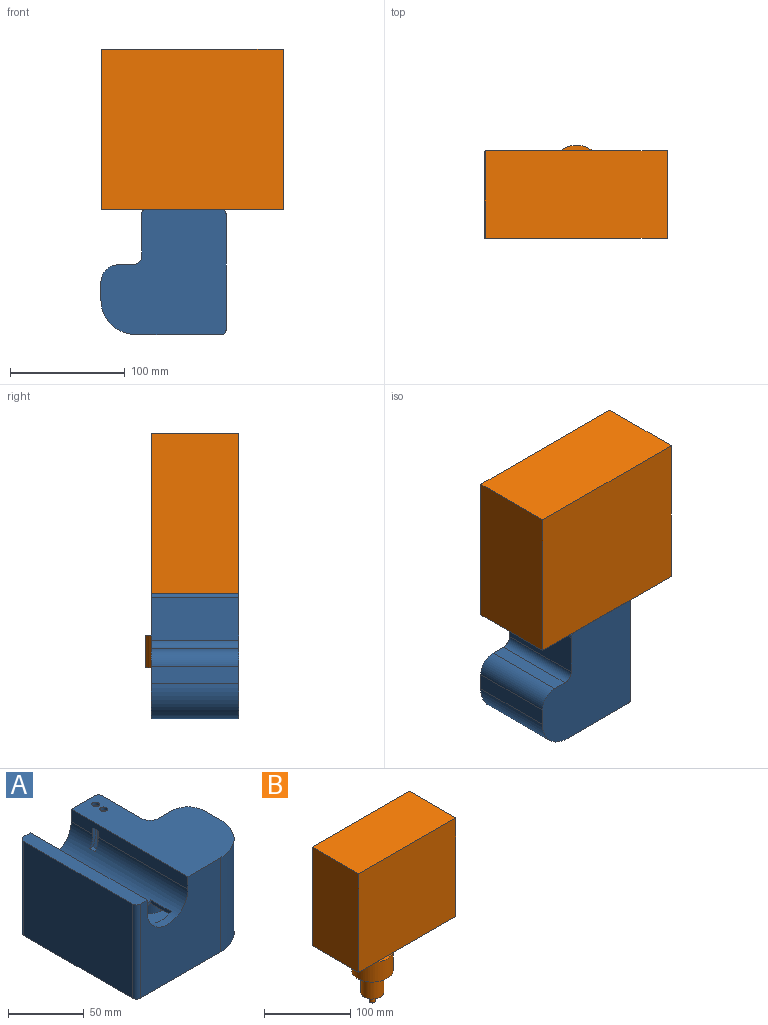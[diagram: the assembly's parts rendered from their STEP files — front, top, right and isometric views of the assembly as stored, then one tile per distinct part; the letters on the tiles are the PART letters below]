
ASSEMBLY  parts=2 mates=1
PART A: 46 faces, bbox 109.2x109.2x76.2 mm
  f0: cylinder r=21.59mm len=104.14mm, axis (0,1,0), area 6633.9mm2, adj f1,f5,f11,f19,f20,f21,f22,f23
  f1: plane 104.14x7.62mm, normal (1,0,0), area 767.7mm2, adj f0,f5,f11,f17,f43,f44,f45
  f2: cylinder r=19.05mm len=109.22mm, axis (0,1,0), area 6102.1mm2, adj f3,f20,f21,f22,f23,f25,f31,f39
  f3: plane 109.22x10.16mm, normal (-1,0,0), area 1083.9mm2, adj f2,f25,f31,f37,f43,f44,f45
  f4: plane 104.14x5.08mm, normal (0,0,-1), area 528.3mm2, adj f5,f8,f9,f10,f11,f19
  f5: plane 71.12x66.04mm, normal (0,-1,0), area 3635.5mm2, adj f0,f1,f4,f7,f8,f17,f18,f19
  f6: plane 71.12x36.83mm, normal (-1,0,0), area 2619.3mm2, adj f7,f16,f17,f18
  f7: cylinder r=1.27mm len=71.12mm, axis (0,0,-1), area 141.9mm2, adj f5,f6,f17,f18
  f8: cylinder r=1.27mm len=71.12mm, axis (0,0,-1), area 141.9mm2, adj f4,f5,f9,f18
  f9: plane 101.6x71.12mm, normal (1,0,0), area 7225.8mm2, adj f4,f8,f10,f18
  f10: cylinder r=1.27mm len=71.12mm, axis (0,0,-1), area 141.9mm2, adj f4,f9,f11,f18
  f11: plane 74.93x71.12mm, normal (0,1,0), area 4267.8mm2, adj f0,f1,f4,f10,f12,f17,f18,f19
  f12: cylinder r=27.94mm len=71.12mm, axis (0,0,-1), area 3121.3mm2, adj f11,f13,f17,f18
  f13: plane 71.12x15.24mm, normal (-1,0,0), area 1083.9mm2, adj f12,f14,f17,f18
  f14: cylinder r=12.7mm len=71.12mm, axis (0,0,-1), area 1418.8mm2, adj f13,f15,f17,f18
  f15: plane 71.12x12.7mm, normal (0,-1,0), area 903.2mm2, adj f14,f16,f17,f18
  f16: cylinder r=10.16mm len=71.12mm, axis (0,0,-1), area 1135mm2, adj f6,f15,f17,f18
  f17: plane 104.14x55.88mm, normal (0,0,-1), area 3882.3mm2, adj f1,f5,f6,f7,f11,f12,f13,f14
  f18: plane 104.14x104.14mm, normal (0,0,1), area 8948mm2, adj f5,f6,f7,f8,f9,f10,f11,f12
  f19: plane 104.14x7.62mm, normal (-1,0,0), area 793.5mm2, adj f0,f4,f5,f11
  f20: plane 19.05x2.88mm, normal (-1,0,0), area 54.8mm2, adj f0,f2,f21,f23
  f21: plane 19.05x5.09mm, normal (0,-1,0), area 50.4mm2, adj f0,f2,f20,f22
  f22: plane 19.05x2.88mm, normal (1,0,0), area 54.8mm2, adj f0,f2,f21,f23
  f23: plane 19.05x5.09mm, normal (0,1,0), area 50.4mm2, adj f0,f2,f20,f22
  f24: plane 109.22x10.16mm, normal (0,0,1), area 1103.4mm2, adj f25,f28,f29,f30,f31,f39
  f25: plane 76.2x66.04mm, normal (0,1,0), area 4075.1mm2, adj f2,f3,f24,f27,f28,f37,f38,f39
  f26: plane 76.2x36.83mm, normal (1,0,0), area 2806.4mm2, adj f27,f36,f37,f38
  f27: cylinder r=3.81mm len=76.2mm, axis (0,0,-1), area 456mm2, adj f25,f26,f37,f38
  f28: cylinder r=3.81mm len=76.2mm, axis (0,0,-1), area 456mm2, adj f24,f25,f29,f38
  f29: plane 101.6x76.2mm, normal (-1,0,0), area 7741.9mm2, adj f24,f28,f30,f38
  f30: cylinder r=3.81mm len=76.2mm, axis (0,0,-1), area 456mm2, adj f24,f29,f31,f38
  f31: plane 76.2x74.93mm, normal (0,-1,0), area 4752.5mm2, adj f2,f3,f24,f30,f32,f37,f38,f39
  f32: cylinder r=30.48mm len=76.2mm, axis (0,0,-1), area 3648.3mm2, adj f31,f33,f37,f38
  f33: plane 76.2x15.24mm, normal (1,0,0), area 1161.3mm2, adj f32,f34,f37,f38
  f34: cylinder r=15.24mm len=76.2mm, axis (0,0,-1), area 1824.1mm2, adj f33,f35,f37,f38
  f35: plane 76.2x12.7mm, normal (0,1,0), area 967.7mm2, adj f34,f36,f37,f38
  f36: cylinder r=7.62mm len=76.2mm, axis (0,0,-1), area 912.1mm2, adj f26,f35,f37,f38
  f37: plane 109.22x60.96mm, normal (0,0,1), area 4661.5mm2, adj f3,f25,f26,f27,f31,f32,f33,f34
  f38: plane 109.22x109.22mm, normal (0,0,-1), area 9966.8mm2, adj f25,f26,f27,f28,f29,f30,f31,f32
  f39: plane 109.22x10.16mm, normal (1,0,0), area 1109.7mm2, adj f2,f24,f25,f31
  f40: cylinder r=2.54mm len=5.08mm, axis (0,0,1), area 40.5mm2, adj f17,f37
  f41: cylinder r=2.54mm len=5.08mm, axis (0,0,1), area 40.5mm2, adj f17,f37
  f42: plane 5.08x2.94mm, normal (0,0,1), area 14.9mm2, adj f0,f2,f43,f44
  f43: plane 15.24x5.48mm, normal (0,1,0), area 39.9mm2, adj f0,f1,f2,f3,f42,f45
  f44: plane 15.24x5.48mm, normal (0,-1,0), area 39.9mm2, adj f0,f1,f2,f3,f42,f45
  f45: plane 5.08x2.54mm, normal (0,0,-1), area 12.9mm2, adj f1,f3,f43,f44
PART B: 14 faces, bbox 158.8x81.3x248.9 mm
  f0: plane 139.7x76.2mm, normal (1,0,0), area 10645.1mm2, adj f1,f3,f4,f5
  f1: plane 158.75x139.7mm, normal (0,1,0), area 22177.4mm2, adj f0,f2,f4,f5
  f2: plane 139.7x76.2mm, normal (-1,0,0), area 10645.1mm2, adj f1,f3,f4,f5
  f3: plane 158.75x139.7mm, normal (0,-1,0), area 22177.4mm2, adj f0,f2,f4,f5
  f4: plane 158.75x76.2mm, normal (0,0,1), area 12096.8mm2, adj f0,f1,f2,f3
  f5: plane 158.75x76.2mm, normal (0,0,-1), area 10956.7mm2, adj f0,f1,f2,f3,f6
  f6: cylinder r=19.05mm len=38.1mm, axis (0,0,1), area 4408.4mm2, adj f5,f9
  f7: cylinder r=24.13mm len=48.26mm, axis (0,0,1), area 4236.1mm2, adj f8,f9
  f8: plane 48.26x48.26mm, normal (0,0,-1), area 1281.2mm2, adj f7,f10
  f9: plane 48.26x48.26mm, normal (0,0,1), area 689.1mm2, adj f6,f7
  f10: cylinder r=13.21mm len=31.75mm, axis (0,0,1), area 2634.9mm2, adj f8,f11
  f11: plane 26.42x26.42mm, normal (0,0,-1), area 516.4mm2, adj f10,f12
  f12: cylinder r=3.17mm len=12.7mm, axis (0,0,1), area 253.4mm2, adj f11,f13
  f13: plane 6.35x6.35mm, normal (0,0,-1), area 31.7mm2, adj f12
PLACE A rot(axis=(0,0.71,0.71),180deg) t=(-25.08,-40.64,-69.85)mm
PLACE B t=(424.56,-40.64,-15.24)mm fixed
MATE fastened A.f25 <-> B.f5  axis (0,0,1) through (-29.53,35.56,-15.24)mm
